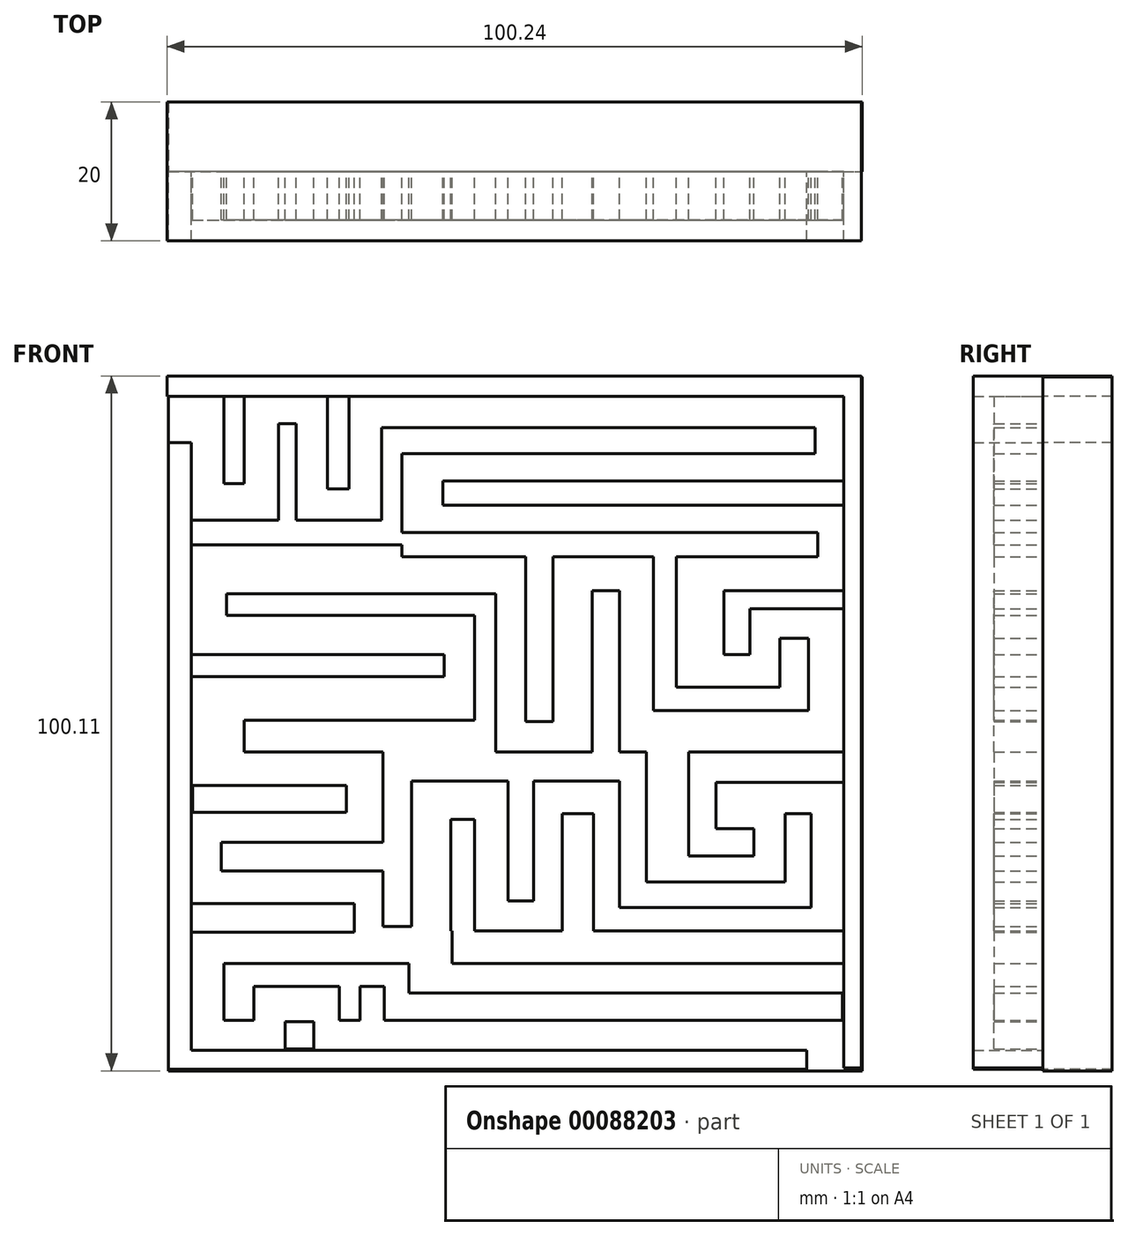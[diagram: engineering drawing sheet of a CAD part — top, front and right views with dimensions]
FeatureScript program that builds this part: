
annotation { "Feature Type Name" : "Feature", "Feature Type Description" : "" }
export const myFeature = defineFeature(function(context is Context, id is Id, definition is map)
    precondition{}
    {
        {
            var Q0;
            Q0=qCreatedBy(makeId("Front.planeOp"),FACE);
            var sketch = newSketch(context, id + "F0", { "sketchPlane" : qUnion([Q0])});
            skLineSegment(sketch, "E0.bottom", {"start": v(-44.12, 54.05) * mm, "end": v(55.88, 54.05) * mm});
            skLineSegment(sketch, "E0.top", {"start": v(-44.12, -45.95) * mm, "end": v(55.88, -45.95) * mm});
            skLineSegment(sketch, "E0.left", {"start": v(-44.12, 54.05) * mm, "end": v(-44.12, -45.95) * mm});
            skLineSegment(sketch, "E0.right", {"start": v(55.88, 54.05) * mm, "end": v(55.88, -45.95) * mm});
            skSolve(sketch);
        }
        {
            var Q0;
            Q0=makeQuery(id+"F0.imprint","IMPRINT",FACE,{"disambiguationData":[TD([[makeQuery(id+"F0.imprint","IMPRINT",EDGE,{"derivedFrom":sQuery(id+"F0.wireOp",EDGE,"E0.bottom")}),-1.0]])]});
            var sketch = newSketch(context, id + "F1", { "sketchPlane" : qUnion([Q0])});
            skLineSegment(sketch, "E1.bottom", {"start": v(-44.36, 54.16) * mm, "end": v(55.72, 54.16) * mm});
            skLineSegment(sketch, "E1.top", {"start": v(-44.36, 51.22) * mm, "end": v(55.72, 51.22) * mm});
            skLineSegment(sketch, "E1.left", {"start": v(-44.36, 54.16) * mm, "end": v(-44.36, 51.22) * mm});
            skLineSegment(sketch, "E1.right", {"start": v(55.72, 54.16) * mm, "end": v(55.72, 51.22) * mm});
            skLineSegment(sketch, "E2.bottom", {"start": v(-44.17, -45.73) * mm, "end": v(-40.84, -45.73) * mm});
            skLineSegment(sketch, "E2.top", {"start": v(-44.17, 44.56) * mm, "end": v(-40.84, 44.56) * mm});
            skLineSegment(sketch, "E2.left", {"start": v(-44.17, -45.73) * mm, "end": v(-44.17, 44.56) * mm});
            skLineSegment(sketch, "E2.right", {"start": v(-40.84, -45.73) * mm, "end": v(-40.84, 44.56) * mm});
            skLineSegment(sketch, "E3.bottom", {"start": v(55.72, 51.22) * mm, "end": v(53.18, 51.22) * mm});
            skLineSegment(sketch, "E3.top", {"start": v(55.72, -45.54) * mm, "end": v(53.18, -45.54) * mm});
            skLineSegment(sketch, "E3.left", {"start": v(55.72, 51.22) * mm, "end": v(55.72, -45.54) * mm});
            skLineSegment(sketch, "E3.right", {"start": v(53.18, 51.22) * mm, "end": v(53.18, -45.54) * mm});
            skLineSegment(sketch, "E4.bottom", {"start": v(-40.84, -45.73) * mm, "end": v(47.89, -45.73) * mm});
            skLineSegment(sketch, "E4.top", {"start": v(-40.84, -43) * mm, "end": v(47.89, -43) * mm});
            skLineSegment(sketch, "E4.left", {"start": v(-40.84, -45.73) * mm, "end": v(-40.84, -43) * mm});
            skLineSegment(sketch, "E4.right", {"start": v(47.89, -45.73) * mm, "end": v(47.89, -43) * mm});
            skSolve(sketch);
        }
        {
            var Q0;
            Q0=makeQuery(id+"F0.imprint","IMPRINT",FACE,{"disambiguationData":[TD([[makeQuery(id+"F0.imprint","IMPRINT",EDGE,{"derivedFrom":sQuery(id+"F0.wireOp",EDGE,"E0.bottom")}),-1.0]])]});
            var sketch = newSketch(context, id + "F2", { "sketchPlane" : qUnion([Q0])});
            skLineSegment(sketch, "E5.bottom", {"start": v(-36.14, 51.22) * mm, "end": v(-33.2, 51.22) * mm});
            skLineSegment(sketch, "E5.top", {"start": v(-36.14, 38.68) * mm, "end": v(-33.2, 38.68) * mm});
            skLineSegment(sketch, "E5.left", {"start": v(-36.14, 51.22) * mm, "end": v(-36.14, 38.68) * mm});
            skLineSegment(sketch, "E5.right", {"start": v(-33.2, 51.22) * mm, "end": v(-33.2, 38.68) * mm});
            skLineSegment(sketch, "E6.bottom", {"start": v(-40.84, 29.87) * mm, "end": v(-10.48, 29.87) * mm});
            skLineSegment(sketch, "E6.top", {"start": v(-40.84, 33.4) * mm, "end": v(-10.48, 33.4) * mm});
            skLineSegment(sketch, "E6.left", {"start": v(-40.84, 29.87) * mm, "end": v(-40.84, 33.4) * mm});
            skLineSegment(sketch, "E6.right", {"start": v(-10.48, 29.87) * mm, "end": v(-10.48, 33.4) * mm});
            skLineSegment(sketch, "E7.bottom", {"start": v(-25.76, 33.4) * mm, "end": v(-28.3, 33.4) * mm});
            skLineSegment(sketch, "E7.top", {"start": v(-25.76, 47.3) * mm, "end": v(-28.3, 47.3) * mm});
            skLineSegment(sketch, "E7.left", {"start": v(-25.76, 33.4) * mm, "end": v(-25.76, 47.3) * mm});
            skLineSegment(sketch, "E7.right", {"start": v(-28.3, 33.4) * mm, "end": v(-28.3, 47.3) * mm});
            skLineSegment(sketch, "E8.bottom", {"start": v(-21.25, 51.22) * mm, "end": v(-18.12, 51.22) * mm});
            skLineSegment(sketch, "E8.top", {"start": v(-21.25, 37.9) * mm, "end": v(-18.12, 37.9) * mm});
            skLineSegment(sketch, "E8.left", {"start": v(-21.25, 51.22) * mm, "end": v(-21.25, 37.9) * mm});
            skLineSegment(sketch, "E8.right", {"start": v(-18.12, 51.22) * mm, "end": v(-18.12, 37.9) * mm});
            skLineSegment(sketch, "E9.bottom", {"start": v(-10.48, 33.4) * mm, "end": v(-13.42, 33.4) * mm});
            skLineSegment(sketch, "E9.top", {"start": v(-10.48, 46.71) * mm, "end": v(-13.42, 46.71) * mm});
            skLineSegment(sketch, "E9.left", {"start": v(-10.48, 33.4) * mm, "end": v(-10.48, 46.71) * mm});
            skLineSegment(sketch, "E9.right", {"start": v(-13.42, 33.4) * mm, "end": v(-13.42, 46.71) * mm});
            skLineSegment(sketch, "E10.bottom", {"start": v(-10.48, 46.71) * mm, "end": v(49.06, 46.71) * mm});
            skLineSegment(sketch, "E10.top", {"start": v(-10.48, 43) * mm, "end": v(49.06, 43) * mm});
            skLineSegment(sketch, "E10.left", {"start": v(-10.48, 46.71) * mm, "end": v(-10.48, 43) * mm});
            skLineSegment(sketch, "E10.right", {"start": v(49.06, 46.71) * mm, "end": v(49.06, 43) * mm});
            skLineSegment(sketch, "E11.bottom", {"start": v(53.18, 39.07) * mm, "end": v(-4.6, 39.07) * mm});
            skLineSegment(sketch, "E11.top", {"start": v(53.18, 35.55) * mm, "end": v(-4.6, 35.55) * mm});
            skLineSegment(sketch, "E11.left", {"start": v(53.18, 39.07) * mm, "end": v(53.18, 35.55) * mm});
            skLineSegment(sketch, "E11.right", {"start": v(-4.6, 39.07) * mm, "end": v(-4.6, 35.55) * mm});
            skLineSegment(sketch, "E12.bottom", {"start": v(-10.48, 31.63) * mm, "end": v(49.46, 31.63) * mm});
            skLineSegment(sketch, "E12.top", {"start": v(-10.48, 28.1) * mm, "end": v(49.46, 28.1) * mm});
            skLineSegment(sketch, "E12.left", {"start": v(-10.48, 31.63) * mm, "end": v(-10.48, 28.1) * mm});
            skLineSegment(sketch, "E12.right", {"start": v(49.46, 31.63) * mm, "end": v(49.46, 28.1) * mm});
            skLineSegment(sketch, "E13.bottom", {"start": v(53.37, 23.2) * mm, "end": v(35.94, 23.2) * mm});
            skLineSegment(sketch, "E13.top", {"start": v(53.37, 20.66) * mm, "end": v(35.94, 20.66) * mm});
            skLineSegment(sketch, "E13.left", {"start": v(53.37, 23.2) * mm, "end": v(53.37, 20.66) * mm});
            skLineSegment(sketch, "E13.right", {"start": v(35.94, 23.2) * mm, "end": v(35.94, 20.66) * mm});
            skLineSegment(sketch, "E14.bottom", {"start": v(25.76, 28.1) * mm, "end": v(29.09, 28.1) * mm});
            skLineSegment(sketch, "E14.top", {"start": v(25.76, 5.97) * mm, "end": v(29.09, 5.97) * mm});
            skLineSegment(sketch, "E14.left", {"start": v(25.76, 28.1) * mm, "end": v(25.76, 5.97) * mm});
            skLineSegment(sketch, "E14.right", {"start": v(29.09, 28.1) * mm, "end": v(29.09, 5.97) * mm});
            skLineSegment(sketch, "E15.bottom", {"start": v(29.09, 5.97) * mm, "end": v(48.08, 5.97) * mm});
            skLineSegment(sketch, "E15.top", {"start": v(29.09, 9.3) * mm, "end": v(48.08, 9.3) * mm});
            skLineSegment(sketch, "E15.left", {"start": v(29.09, 5.97) * mm, "end": v(29.09, 9.3) * mm});
            skLineSegment(sketch, "E15.right", {"start": v(48.08, 5.97) * mm, "end": v(48.08, 9.3) * mm});
            skLineSegment(sketch, "E16.bottom", {"start": v(35.94, 20.66) * mm, "end": v(39.66, 20.66) * mm});
            skLineSegment(sketch, "E16.top", {"start": v(35.94, 14) * mm, "end": v(39.66, 14) * mm});
            skLineSegment(sketch, "E16.left", {"start": v(35.94, 20.66) * mm, "end": v(35.94, 14) * mm});
            skLineSegment(sketch, "E16.right", {"start": v(39.66, 20.66) * mm, "end": v(39.66, 14) * mm});
            skLineSegment(sketch, "E17.bottom", {"start": v(48.08, 9.3) * mm, "end": v(43.97, 9.3) * mm});
            skLineSegment(sketch, "E17.top", {"start": v(48.08, 16.35) * mm, "end": v(43.97, 16.35) * mm});
            skLineSegment(sketch, "E17.left", {"start": v(48.08, 9.3) * mm, "end": v(48.08, 16.35) * mm});
            skLineSegment(sketch, "E17.right", {"start": v(43.97, 9.3) * mm, "end": v(43.97, 16.35) * mm});
            skLineSegment(sketch, "E18.bottom", {"start": v(53.37, 0) * mm, "end": v(30.85, 0) * mm});
            skLineSegment(sketch, "E18.top", {"start": v(53.37, -4.4) * mm, "end": v(30.85, -4.4) * mm});
            skLineSegment(sketch, "E18.left", {"start": v(53.37, 0) * mm, "end": v(53.37, -4.4) * mm});
            skLineSegment(sketch, "E18.right", {"start": v(30.85, 0) * mm, "end": v(30.85, -4.4) * mm});
            skLineSegment(sketch, "E19.bottom", {"start": v(24.78, 0) * mm, "end": v(20.86, 0) * mm});
            skLineSegment(sketch, "E19.top", {"start": v(24.78, -22.43) * mm, "end": v(20.86, -22.43) * mm});
            skLineSegment(sketch, "E19.left", {"start": v(24.78, 0) * mm, "end": v(24.78, -22.43) * mm});
            skLineSegment(sketch, "E19.right", {"start": v(20.86, 0) * mm, "end": v(20.86, -22.43) * mm});
            skLineSegment(sketch, "E20.bottom", {"start": v(24.78, -22.43) * mm, "end": v(48.48, -22.43) * mm});
            skLineSegment(sketch, "E20.top", {"start": v(24.78, -18.7) * mm, "end": v(48.48, -18.7) * mm});
            skLineSegment(sketch, "E20.left", {"start": v(24.78, -22.43) * mm, "end": v(24.78, -18.7) * mm});
            skLineSegment(sketch, "E20.right", {"start": v(48.48, -22.43) * mm, "end": v(48.48, -18.7) * mm});
            skLineSegment(sketch, "E21.bottom", {"start": v(30.85, -4.4) * mm, "end": v(34.77, -4.4) * mm});
            skLineSegment(sketch, "E21.top", {"start": v(30.85, -14.98) * mm, "end": v(34.77, -14.98) * mm});
            skLineSegment(sketch, "E21.left", {"start": v(30.85, -4.4) * mm, "end": v(30.85, -14.98) * mm});
            skLineSegment(sketch, "E21.right", {"start": v(34.77, -4.4) * mm, "end": v(34.77, -14.98) * mm});
            skLineSegment(sketch, "E22.bottom", {"start": v(34.77, -14.98) * mm, "end": v(40.25, -14.98) * mm});
            skLineSegment(sketch, "E22.top", {"start": v(34.77, -11.07) * mm, "end": v(40.25, -11.07) * mm});
            skLineSegment(sketch, "E22.left", {"start": v(34.77, -14.98) * mm, "end": v(34.77, -11.07) * mm});
            skLineSegment(sketch, "E22.right", {"start": v(40.25, -14.98) * mm, "end": v(40.25, -11.07) * mm});
            skLineSegment(sketch, "E23.bottom", {"start": v(48.48, -18.7) * mm, "end": v(44.75, -18.7) * mm});
            skLineSegment(sketch, "E23.top", {"start": v(48.48, -8.91) * mm, "end": v(44.75, -8.91) * mm});
            skLineSegment(sketch, "E23.left", {"start": v(48.48, -18.7) * mm, "end": v(48.48, -8.91) * mm});
            skLineSegment(sketch, "E23.right", {"start": v(44.75, -18.7) * mm, "end": v(44.75, -8.91) * mm});
            skLineSegment(sketch, "E24.bottom", {"start": v(20.86, 0) * mm, "end": v(16.94, 0) * mm});
            skLineSegment(sketch, "E24.top", {"start": v(20.86, 23.2) * mm, "end": v(16.94, 23.2) * mm});
            skLineSegment(sketch, "E24.left", {"start": v(20.86, 0) * mm, "end": v(20.86, 23.2) * mm});
            skLineSegment(sketch, "E24.right", {"start": v(16.94, 0) * mm, "end": v(16.94, 23.2) * mm});
            skLineSegment(sketch, "E25.bottom", {"start": v(11.26, 28.1) * mm, "end": v(7.34, 28.1) * mm});
            skLineSegment(sketch, "E25.top", {"start": v(11.26, 4.4) * mm, "end": v(7.34, 4.4) * mm});
            skLineSegment(sketch, "E25.left", {"start": v(11.26, 28.1) * mm, "end": v(11.26, 4.4) * mm});
            skLineSegment(sketch, "E25.right", {"start": v(7.34, 28.1) * mm, "end": v(7.34, 4.4) * mm});
            skLineSegment(sketch, "E26.bottom", {"start": v(20.86, 0) * mm, "end": v(0, 0) * mm});
            skLineSegment(sketch, "E26.top", {"start": v(20.86, -4.21) * mm, "end": v(0, -4.21) * mm});
            skLineSegment(sketch, "E26.left", {"start": v(20.86, 0) * mm, "end": v(20.86, -4.21) * mm});
            skLineSegment(sketch, "E26.right", {"start": v(0, 0) * mm, "end": v(0, -4.21) * mm});
            skLineSegment(sketch, "E27.bottom", {"start": v(0, 0) * mm, "end": v(3.04, 0) * mm});
            skLineSegment(sketch, "E27.top", {"start": v(0, 22.82) * mm, "end": v(3.04, 22.82) * mm});
            skLineSegment(sketch, "E27.left", {"start": v(0, 0) * mm, "end": v(0, 22.82) * mm});
            skLineSegment(sketch, "E27.right", {"start": v(3.04, 0) * mm, "end": v(3.04, 22.82) * mm});
            skLineSegment(sketch, "E28.bottom", {"start": v(53.18, -25.76) * mm, "end": v(12.63, -25.76) * mm});
            skLineSegment(sketch, "E28.top", {"start": v(53.18, -30.46) * mm, "end": v(12.63, -30.46) * mm});
            skLineSegment(sketch, "E28.left", {"start": v(53.18, -25.76) * mm, "end": v(53.18, -30.46) * mm});
            skLineSegment(sketch, "E28.right", {"start": v(12.63, -25.76) * mm, "end": v(12.63, -30.46) * mm});
            skLineSegment(sketch, "E29.bottom", {"start": v(12.63, -25.76) * mm, "end": v(17.14, -25.76) * mm});
            skLineSegment(sketch, "E29.top", {"start": v(12.63, -8.91) * mm, "end": v(17.14, -8.91) * mm});
            skLineSegment(sketch, "E29.left", {"start": v(12.63, -25.76) * mm, "end": v(12.63, -8.91) * mm});
            skLineSegment(sketch, "E29.right", {"start": v(17.14, -25.76) * mm, "end": v(17.14, -8.91) * mm});
            skLineSegment(sketch, "E30.bottom", {"start": v(4.8, -4.21) * mm, "end": v(8.52, -4.21) * mm});
            skLineSegment(sketch, "E30.top", {"start": v(4.8, -21.45) * mm, "end": v(8.52, -21.45) * mm});
            skLineSegment(sketch, "E30.left", {"start": v(4.8, -4.21) * mm, "end": v(4.8, -21.45) * mm});
            skLineSegment(sketch, "E30.right", {"start": v(8.52, -4.21) * mm, "end": v(8.52, -21.45) * mm});
            skLineSegment(sketch, "E31.bottom", {"start": v(12.63, -25.76) * mm, "end": v(-3.23, -25.76) * mm});
            skLineSegment(sketch, "E31.top", {"start": v(12.63, -30.46) * mm, "end": v(-3.23, -30.46) * mm});
            skLineSegment(sketch, "E31.right", {"start": v(-3.23, -25.76) * mm, "end": v(-3.23, -30.46) * mm});
            skLineSegment(sketch, "E32.bottom", {"start": v(0, -25.76) * mm, "end": v(-3.43, -25.76) * mm});
            skLineSegment(sketch, "E32.top", {"start": v(0, -9.7) * mm, "end": v(-3.43, -9.7) * mm});
            skLineSegment(sketch, "E32.left", {"start": v(0, -25.76) * mm, "end": v(0, -9.7) * mm});
            skLineSegment(sketch, "E32.right", {"start": v(-3.43, -25.76) * mm, "end": v(-3.43, -9.7) * mm});
            skLineSegment(sketch, "E33.bottom", {"start": v(0, -4.21) * mm, "end": v(-13.22, -4.21) * mm});
            skLineSegment(sketch, "E33.top", {"start": v(0, 0) * mm, "end": v(-13.22, 0) * mm});
            skLineSegment(sketch, "E33.left", {"start": v(0, -4.21) * mm, "end": v(0, 0) * mm});
            skLineSegment(sketch, "E33.right", {"start": v(-13.22, -4.21) * mm, "end": v(-13.22, 0) * mm});
            skLineSegment(sketch, "E34.bottom", {"start": v(-13.22, -4.21) * mm, "end": v(-9.1, -4.21) * mm});
            skLineSegment(sketch, "E34.top", {"start": v(-13.22, -25.17) * mm, "end": v(-9.1, -25.17) * mm});
            skLineSegment(sketch, "E34.left", {"start": v(-13.22, -4.21) * mm, "end": v(-13.22, -25.17) * mm});
            skLineSegment(sketch, "E34.right", {"start": v(-9.1, -4.21) * mm, "end": v(-9.1, -25.17) * mm});
            skLineSegment(sketch, "E35.bottom", {"start": v(-13.02, -30.46) * mm, "end": v(-9.5, -30.46) * mm});
            skLineSegment(sketch, "E35.top", {"start": v(-13.02, -38.68) * mm, "end": v(-9.5, -38.68) * mm});
            skLineSegment(sketch, "E35.left", {"start": v(-13.02, -30.46) * mm, "end": v(-13.02, -38.68) * mm});
            skLineSegment(sketch, "E35.right", {"start": v(-9.5, -30.46) * mm, "end": v(-9.5, -38.68) * mm});
            skLineSegment(sketch, "E36.bottom", {"start": v(-9.5, -38.68) * mm, "end": v(52.98, -38.68) * mm});
            skLineSegment(sketch, "E36.top", {"start": v(-9.5, -34.77) * mm, "end": v(52.98, -34.77) * mm});
            skLineSegment(sketch, "E36.left", {"start": v(-9.5, -38.68) * mm, "end": v(-9.5, -34.77) * mm});
            skLineSegment(sketch, "E36.right", {"start": v(52.98, -38.68) * mm, "end": v(52.98, -34.77) * mm});
            skLineSegment(sketch, "E37.bottom", {"start": v(0, 22.82) * mm, "end": v(-35.74, 22.82) * mm});
            skLineSegment(sketch, "E37.top", {"start": v(0, 19.68) * mm, "end": v(-35.74, 19.68) * mm});
            skLineSegment(sketch, "E37.left", {"start": v(0, 22.82) * mm, "end": v(0, 19.68) * mm});
            skLineSegment(sketch, "E37.right", {"start": v(-35.74, 22.82) * mm, "end": v(-35.74, 19.68) * mm});
            skLineSegment(sketch, "E38.bottom", {"start": v(-40.84, 14) * mm, "end": v(-4.4, 14) * mm});
            skLineSegment(sketch, "E38.top", {"start": v(-40.84, 10.87) * mm, "end": v(-4.4, 10.87) * mm});
            skLineSegment(sketch, "E38.left", {"start": v(-40.84, 14) * mm, "end": v(-40.84, 10.87) * mm});
            skLineSegment(sketch, "E38.right", {"start": v(-4.4, 14) * mm, "end": v(-4.4, 10.87) * mm});
            skLineSegment(sketch, "E39.bottom", {"start": v(0, 0) * mm, "end": v(-33.2, 0) * mm});
            skLineSegment(sketch, "E39.top", {"start": v(0, 4.6) * mm, "end": v(-33.2, 4.6) * mm});
            skLineSegment(sketch, "E39.left", {"start": v(0, 0) * mm, "end": v(0, 4.6) * mm});
            skLineSegment(sketch, "E39.right", {"start": v(-33.2, 0) * mm, "end": v(-33.2, 4.6) * mm});
            skLineSegment(sketch, "E40.bottom", {"start": v(-40.64, -4.8) * mm, "end": v(-18.5, -4.8) * mm});
            skLineSegment(sketch, "E40.top", {"start": v(-40.64, -8.72) * mm, "end": v(-18.5, -8.72) * mm});
            skLineSegment(sketch, "E40.left", {"start": v(-40.64, -4.8) * mm, "end": v(-40.64, -8.72) * mm});
            skLineSegment(sketch, "E40.right", {"start": v(-18.5, -4.8) * mm, "end": v(-18.5, -8.72) * mm});
            skLineSegment(sketch, "E41.bottom", {"start": v(-13.22, -13.02) * mm, "end": v(-36.53, -13.02) * mm});
            skLineSegment(sketch, "E41.top", {"start": v(-13.22, -17.14) * mm, "end": v(-36.53, -17.14) * mm});
            skLineSegment(sketch, "E41.left", {"start": v(-13.22, -13.02) * mm, "end": v(-13.22, -17.14) * mm});
            skLineSegment(sketch, "E41.right", {"start": v(-36.53, -13.02) * mm, "end": v(-36.53, -17.14) * mm});
            skLineSegment(sketch, "E42.bottom", {"start": v(-40.84, -21.84) * mm, "end": v(-17.33, -21.84) * mm});
            skLineSegment(sketch, "E42.top", {"start": v(-40.84, -25.95) * mm, "end": v(-17.33, -25.95) * mm});
            skLineSegment(sketch, "E42.left", {"start": v(-40.84, -21.84) * mm, "end": v(-40.84, -25.95) * mm});
            skLineSegment(sketch, "E42.right", {"start": v(-17.33, -21.84) * mm, "end": v(-17.33, -25.95) * mm});
            skLineSegment(sketch, "E43.bottom", {"start": v(-13.02, -30.46) * mm, "end": v(-36.14, -30.46) * mm});
            skLineSegment(sketch, "E43.top", {"start": v(-13.02, -33.79) * mm, "end": v(-36.14, -33.79) * mm});
            skLineSegment(sketch, "E43.left", {"start": v(-13.02, -30.46) * mm, "end": v(-13.02, -33.79) * mm});
            skLineSegment(sketch, "E43.right", {"start": v(-36.14, -30.46) * mm, "end": v(-36.14, -33.79) * mm});
            skLineSegment(sketch, "E44.bottom", {"start": v(-36.14, -33.79) * mm, "end": v(-31.83, -33.79) * mm});
            skLineSegment(sketch, "E44.top", {"start": v(-36.14, -38.68) * mm, "end": v(-31.83, -38.68) * mm});
            skLineSegment(sketch, "E44.left", {"start": v(-36.14, -33.79) * mm, "end": v(-36.14, -38.68) * mm});
            skLineSegment(sketch, "E44.right", {"start": v(-31.83, -33.79) * mm, "end": v(-31.83, -38.68) * mm});
            skLineSegment(sketch, "E45.bottom", {"start": v(-27.32, -42.8) * mm, "end": v(-23.2, -42.8) * mm});
            skLineSegment(sketch, "E45.top", {"start": v(-27.32, -38.88) * mm, "end": v(-23.2, -38.88) * mm});
            skLineSegment(sketch, "E45.left", {"start": v(-27.32, -42.8) * mm, "end": v(-27.32, -38.88) * mm});
            skLineSegment(sketch, "E45.right", {"start": v(-23.2, -42.8) * mm, "end": v(-23.2, -38.88) * mm});
            skLineSegment(sketch, "E46.bottom", {"start": v(-19.49, -33.79) * mm, "end": v(-16.55, -33.79) * mm});
            skLineSegment(sketch, "E46.top", {"start": v(-19.49, -38.68) * mm, "end": v(-16.55, -38.68) * mm});
            skLineSegment(sketch, "E46.left", {"start": v(-19.49, -33.79) * mm, "end": v(-19.49, -38.68) * mm});
            skLineSegment(sketch, "E46.right", {"start": v(-16.55, -33.79) * mm, "end": v(-16.55, -38.68) * mm});
            skSolve(sketch);
        }
        {
            var Q0;
            Q0 = qSketchRegion(id + "F0", true);
            extrude(context, id + "F3", {"entities" : qUnion([Q0]), "depth" : 10 * mm});
        }
        {
            var Q0;
            Q0 = qSketchRegion(id + "F1", true);
            extrude(context, id + "F4", {"entities" : qUnion([Q0]), "operationType" : NewBodyOperationType.ADD, "depth" : 20 * mm});
        }
        {
            var Q0;
            Q0 = qSketchRegion(id + "F2", true);
            extrude(context, id + "F5", {"entities" : qUnion([Q0]), "operationType" : NewBodyOperationType.ADD, "depth" : 17 * mm});
        }
    });
